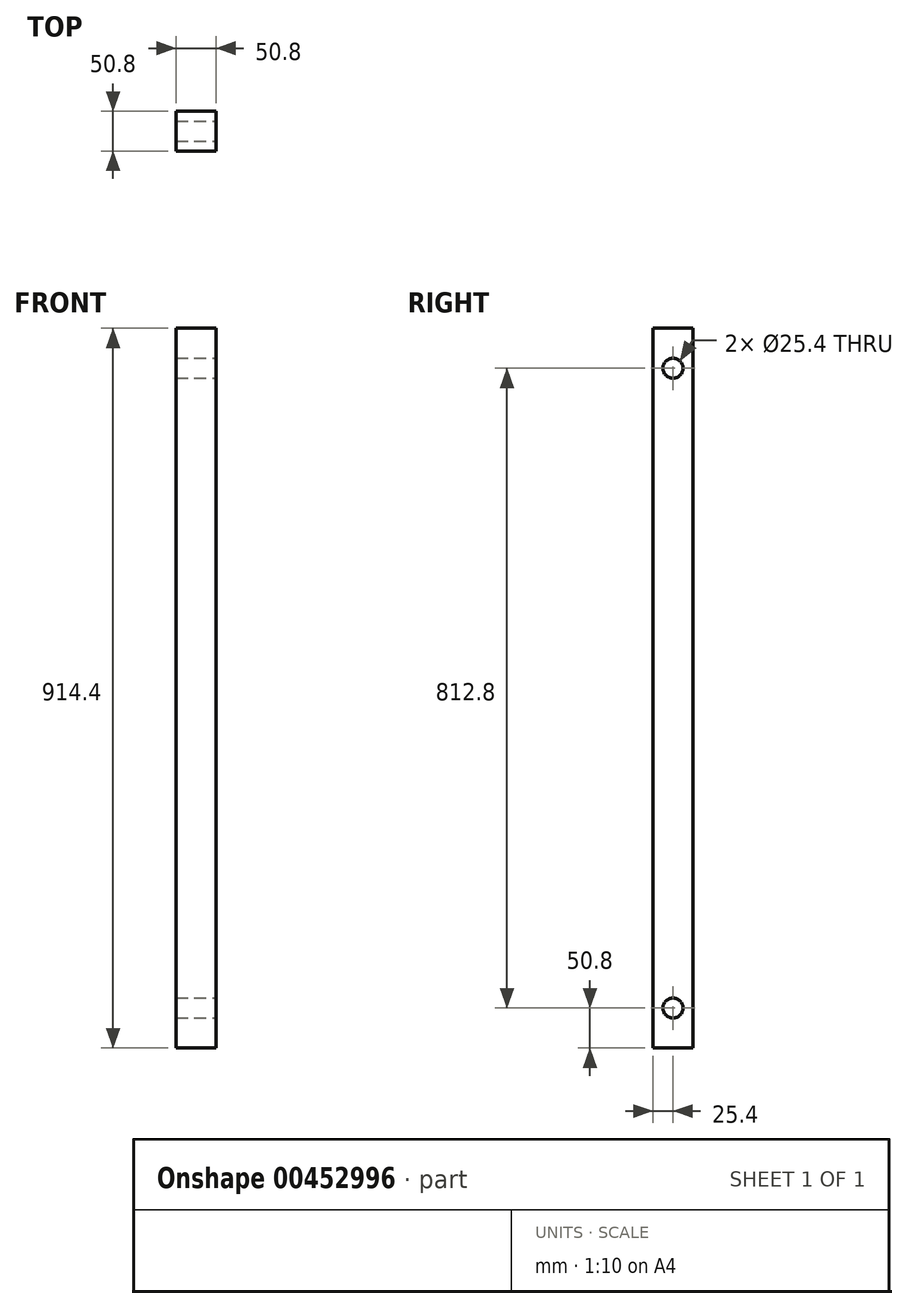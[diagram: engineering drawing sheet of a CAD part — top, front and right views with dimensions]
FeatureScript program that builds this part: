
annotation { "Feature Type Name" : "Feature", "Feature Type Description" : "" }
export const myFeature = defineFeature(function(context is Context, id is Id, definition is map)
    precondition{}
    {
        {
            var Q0;
            Q0=qCreatedBy(makeId("Right.planeOp"),FACE);
            var sketch = newSketch(context, id + "F0", { "sketchPlane" : qUnion([Q0])});
            skLineSegment(sketch, "E0.bottom", {"start": v(25.4, -457.2) * mm, "end": v(-25.4, -457.2) * mm});
            skLineSegment(sketch, "E0.top", {"start": v(25.4, 457.2) * mm, "end": v(-25.4, 457.2) * mm});
            skLineSegment(sketch, "E0.left", {"start": v(25.4, -457.2) * mm, "end": v(25.4, 457.2) * mm});
            skLineSegment(sketch, "E0.right", {"start": v(-25.4, -457.2) * mm, "end": v(-25.4, 457.2) * mm});
            skPoint(sketch, "E0.middle", {"position": v(0, 0) * mm});
            skPoint(sketch, "E1", {"position": v(0, -406.4) * mm});
            skPoint(sketch, "E1.positionSnap0", {"position": v(0, -457.2) * mm});
            skPoint(sketch, "E2.MirrorP", {"position": v(0, 406.4) * mm});
            skPoint(sketch, "E3", {"position": v(0, -203.2) * mm});
            skPoint(sketch, "E4.MirrorP", {"position": v(0, 203.2) * mm});
            skSolve(sketch);
        }
        {
            var Q0;
            Q0=makeQuery(id+"F0.imprint","IMPRINT",FACE,{"disambiguationData":[TD([[makeQuery(id+"F0.imprint","IMPRINT",EDGE,{"derivedFrom":sQuery(id+"F0.wireOp",EDGE,"E0.bottom")}),-1.0]])]});
            extrude(context, id + "F1", {"entities" : qUnion([Q0]), "depth" : 50.8 * mm});
        }
        {
            var Q0;
            Q0=sQuery(id+"F0.wireOp",VERTEX,"E2.MirrorP");
            var Q1;
            Q1=sQuery(id+"F0.wireOp",VERTEX,"E1");
            var Q2;
            Q2=makeQuery(id+"F1.opExtrude","SWEPT_BODY",BODY,{"disambiguationData":[OSD([sQuery(id+"F0.wireOp",EDGE,"E0.bottom"),sQuery(id+"F0.wireOp",EDGE,"E0.top"),sQuery(id+"F0.wireOp",EDGE,"E0.left"),sQuery(id+"F0.wireOp",EDGE,"E0.right")])]});
            hole(context, id + "F2", {"style" : HoleStyle.SIMPLE, "endStyle" : HoleEndStyle.THROUGH, "oppositeDirection" : true, "holeDiameter" : 25.4 * mm, "isTappedThrough" : true, "tappedDepth" : 12.7 * mm, "tapClearance" : 3, "locations" : qUnion([Q0, Q1]), "scope" : qUnion([Q2]), "startStyle" : HoleStartStyle.PART});
        }
    });
